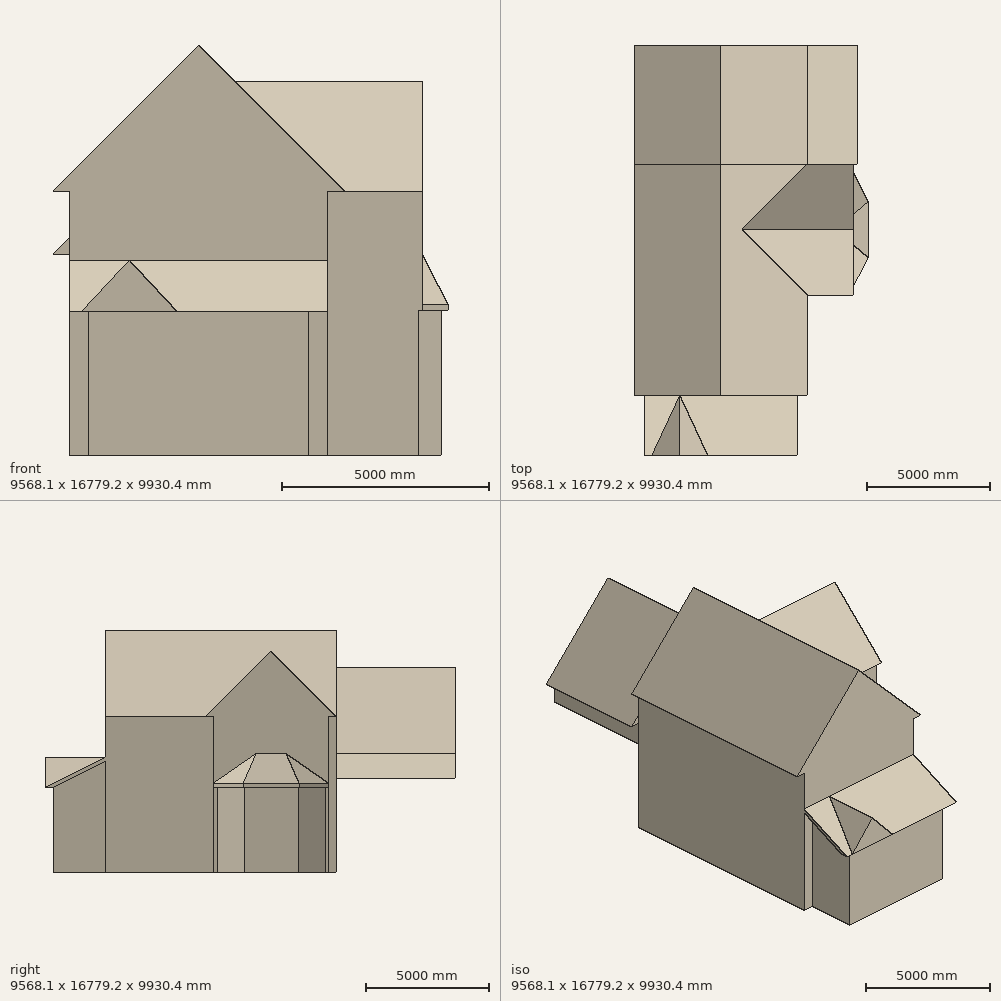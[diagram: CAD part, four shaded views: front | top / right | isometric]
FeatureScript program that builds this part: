
annotation { "Feature Type Name" : "Feature", "Feature Type Description" : "" }
export const myFeature = defineFeature(function(context is Context, id is Id, definition is map)
    precondition{}
    {
        {
            var Q0;
            Q0=qCreatedBy(makeId("Front.planeOp"),FACE);
            var sketch = newSketch(context, id + "F0", { "sketchPlane" : qUnion([Q0])});
            skLineSegment(sketch, "E0", {"start": v(-3529.58, 0) * mm, "end": v(0, 3529.58) * mm});
            skLineSegment(sketch, "E1", {"start": v(0, 3529.58) * mm, "end": v(3529.58, 0) * mm});
            skLineSegment(sketch, "E2", {"start": v(3529.58, 0) * mm, "end": v(-3529.58, 0) * mm});
            skLineSegment(sketch, "E3", {"start": v(0, 0) * mm, "end": v(0, 3529.58) * mm, "construction": true});
            skLineSegment(sketch, "E4", {"start": v(-3124.2, 0) * mm, "end": v(-3124.2, -696.38) * mm, "construction": true});
            skLineSegment(sketch, "E5", {"start": v(-3124.2, -696.38) * mm, "end": v(3124.2, -696.38) * mm, "construction": true});
            skLineSegment(sketch, "E6", {"start": v(3124.2, -696.38) * mm, "end": v(3124.2, 0) * mm, "construction": true});
            skSolve(sketch);
        }
        {
            var Q0;
            Q0=makeQuery(id+"F0.imprint","IMPRINT",FACE,{"disambiguationData":[TD([[makeQuery(id+"F0.imprint","IMPRINT",EDGE,{"derivedFrom":sQuery(id+"F0.wireOp",EDGE,"E0")}),-1.0]])]});
            extrude(context, id + "F1", {"entities" : qUnion([Q0]), "oppositeDirection" : true, "depth" : 9448.8 * mm, "offsetDistance" : 30.48 * mm});
        }
        {
            var Q0;
            Q0=makeQuery(id+"F1.opExtrude","CAP_FACE",FACE,{"disambiguationData":[OSD([sQuery(id+"F0.wireOp",EDGE,"E0"),sQuery(id+"F0.wireOp",EDGE,"E1"),sQuery(id+"F0.wireOp",EDGE,"E2")])],"isStart":false});
            var sketch = newSketch(context, id + "F2", { "sketchPlane" : qUnion([Q0])});
            skLineSegment(sketch, "E7", {"start": v(3529.58, -1524) * mm, "end": v(0, 2005.58) * mm});
            skLineSegment(sketch, "E8", {"start": v(0, 2005.58) * mm, "end": v(-3529.58, -1524) * mm});
            skLineSegment(sketch, "E9", {"start": v(0, 2005.58) * mm, "end": v(0, 3529.58) * mm, "construction": true});
            skLineSegment(sketch, "E10", {"start": v(3529.58, -1524) * mm, "end": v(3529.58, 0) * mm, "construction": true});
            skLineSegment(sketch, "E11", {"start": v(-3529.58, -1524) * mm, "end": v(3529.58, -1524) * mm, "construction": true});
            skLineSegment(sketch, "E12", {"start": v(-3529.58, -1524) * mm, "end": v(-5574.24, -2546.33) * mm});
            skLineSegment(sketch, "E13", {"start": v(-5574.24, -2546.33) * mm, "end": v(3072.38, -2546.33) * mm});
            skLineSegment(sketch, "E14", {"start": v(3072.38, -2546.33) * mm, "end": v(3072.38, -1524) * mm});
            skLineSegment(sketch, "E15", {"start": v(3072.38, -1524) * mm, "end": v(3529.58, -1524) * mm});
            skLineSegment(sketch, "E16", {"start": v(-5269.44, -2546.33) * mm, "end": v(-5269.44, -2393.93) * mm, "construction": true});
            skLineSegment(sketch, "E17", {"start": v(-3529.58, -1524) * mm, "end": v(-3529.58, 0) * mm, "construction": true});
            skSolve(sketch);
        }
        {
            var Q0;
            Q0=qSketchRegion(id+"F2",true);
            extrude(context, id + "F3", {"entities" : qUnion([Q0]), "operationType" : NewBodyOperationType.ADD, "depth" : 4876.8 * mm, "offsetDistance" : 30.48 * mm});
        }
        {
            var Q0;
            Q0=makeQuery(id+"F1.opExtrude","SWEPT_FACE",FACE,{"disambiguationData":[OSD([sQuery(id+"F0.wireOp",EDGE,"E2")])]});
            var sketch = newSketch(context, id + "F4", { "sketchPlane" : qUnion([Q0])});
            skLineSegment(sketch, "E18", {"start": v(-3124.2, 0) * mm, "end": v(-3124.2, -9448.8) * mm});
            skLineSegment(sketch, "E19", {"start": v(-3124.2, -9448.8) * mm, "end": v(3124.2, -9448.8) * mm});
            skLineSegment(sketch, "E20", {"start": v(3124.2, -9448.8) * mm, "end": v(3124.2, 0) * mm});
            skLineSegment(sketch, "E21", {"start": v(3124.2, 0) * mm, "end": v(-3124.2, 0) * mm});
            skLineSegment(sketch, "E22", {"start": v(-3124.2, -4724.4) * mm, "end": v(-3529.58, -4724.4) * mm, "construction": true});
            skLineSegment(sketch, "E23", {"start": v(3124.2, -4724.4) * mm, "end": v(3529.58, -4724.4) * mm, "construction": true});
            skSolve(sketch);
        }
        {
            var Q0;
            Q0=qSketchRegion(id+"F4",true);
            extrude(context, id + "F5", {"entities" : qUnion([Q0]), "operationType" : NewBodyOperationType.ADD, "depth" : 6400.8 * mm, "offsetDistance" : 30.48 * mm});
        }
        {
            var Q0;
            Q0=makeQuery(id+"F5.opExtrude","SWEPT_FACE",FACE,{"disambiguationData":[OSD([sQuery(id+"F4.wireOp",EDGE,"E20")])]});
            var sketch = newSketch(context, id + "F6", { "sketchPlane" : qUnion([Q0])});
            skLineSegment(sketch, "E24", {"start": v(4114.8, 0) * mm, "end": v(6781.8, 2667) * mm});
            skLineSegment(sketch, "E25", {"start": v(6781.8, 2667) * mm, "end": v(9448.8, 0) * mm});
            skLineSegment(sketch, "E26", {"start": v(9448.8, 0) * mm, "end": v(4114.8, 0) * mm});
            skLineSegment(sketch, "E27", {"start": v(6781.8, 0) * mm, "end": v(6781.8, 2667) * mm, "construction": true});
            skSolve(sketch);
        }
        {
            var Q0;
            Q0=qSketchRegion(id+"F6",true);
            var Q1;
            Q1=makeQuery(id+"F1.opExtrude","SWEPT_FACE",FACE,{"disambiguationData":[OSD([sQuery(id+"F0.wireOp",EDGE,"E1")])]});
            extrude(context, id + "F7", {"entities" : qUnion([Q0]), "operationType" : NewBodyOperationType.ADD, "depth" : 2286 * mm, "offsetDistance" : 30.48 * mm, "hasSecondDirection" : true, "secondDirectionBound" : SecondDirectionBoundingType.UP_TO_SURFACE, "secondDirectionOppositeDirection" : true, "secondDirectionDepth" : 30.48 * mm, "secondDirectionBoundEntityFace" : qUnion([Q1])});
        }
        {
            var Q0;
            {var subQ0=sQuery(id+"F0.wireOp",EDGE,"E1");var subQ1=sQuery(id+"F0.wireOp",EDGE,"E2");Q0=makeQuery(id+"F7.boolean.opBoolean","MERGE",FACE,{"derivedFrom":[makeQuery(id+"F5.boolean.opBoolean","SPLIT",FACE,{"disambiguationData":[TD([makeQuery(id+"F1.opExtrude","SWEPT_FACE",FACE,{"disambiguationData":[OSD([subQ0])]})])],"derivedFrom":makeQuery(id+"F1.opExtrude","SWEPT_FACE",FACE,{"disambiguationData":[OSD([subQ1])]})}),makeQuery(id+"F7.opExtrude","SWEPT_FACE",FACE,{"disambiguationData":[OSD([sQuery(id+"F6.wireOp",EDGE,"E26")])]})]});}
            var sketch = newSketch(context, id + "F8", { "sketchPlane" : qUnion([Q0])});
            skLineSegment(sketch, "E28", {"start": v(5410.2, -4419.6) * mm, "end": v(3124.2, -4419.6) * mm});
            skLineSegment(sketch, "E29", {"start": v(3124.2, -4419.6) * mm, "end": v(3124.2, -9144) * mm});
            skLineSegment(sketch, "E30", {"start": v(3124.2, -9144) * mm, "end": v(5410.2, -9144) * mm});
            skLineSegment(sketch, "E31", {"start": v(5410.2, -9144) * mm, "end": v(5410.2, -4419.6) * mm});
            skPoint(sketch, "E32.endSnap0", {"position": v(4267.2, -9144) * mm});
            skLineSegment(sketch, "E33", {"start": v(4267.2, -9448.8) * mm, "end": v(4267.2, -4114.8) * mm, "construction": true});
            skLineSegment(sketch, "E34", {"start": v(4267.2, -6781.8) * mm, "end": v(5410.2, -6781.8) * mm, "construction": true});
            skSolve(sketch);
        }
        {
            var Q0;
            Q0=qSketchRegion(id+"F8",true);
            var Q1;
            Q1=makeQuery(id+"F5.opExtrude","CAP_FACE",FACE,{"disambiguationData":[OSD([sQuery(id+"F4.wireOp",EDGE,"E18"),sQuery(id+"F4.wireOp",EDGE,"E19"),sQuery(id+"F4.wireOp",EDGE,"E20"),sQuery(id+"F4.wireOp",EDGE,"E21")])],"isStart":false});
            extrude(context, id + "F9", {"entities" : qUnion([Q0]), "operationType" : NewBodyOperationType.ADD, "endBound" : BoundingType.UP_TO_SURFACE, "depth" : 30.48 * mm, "endBoundEntityFace" : qUnion([Q1]), "offsetDistance" : 30.48 * mm});
        }
        {
            var Q0;
            {var subQ0=sQuery(id+"F4.wireOp",EDGE,"E21");var subQ1=sQuery(id+"F4.wireOp",EDGE,"E20");Q0=makeQuery(id+"F12.boolean.opBoolean","MERGE",FACE,{"derivedFrom":[makeQuery(id+"F9.boolean.opBoolean","SPLIT",FACE,{"disambiguationData":[TD([makeQuery(id+"F5.opExtrude","SWEPT_FACE",FACE,{"disambiguationData":[OSD([subQ0])]})])],"derivedFrom":makeQuery(id+"F5.opExtrude","SWEPT_FACE",FACE,{"disambiguationData":[OSD([subQ1])]})}),makeQuery(id+"F12.opExtrude","CAP_FACE",FACE,{"disambiguationData":[OSD([sQuery(id+"F11.wireOp",EDGE,"E35"),sQuery(id+"F11.wireOp",EDGE,"E36"),sQuery(id+"F11.wireOp",EDGE,"E37"),sQuery(id+"F11.wireOp",EDGE,"E38"),sQuery(id+"F11.wireOp",EDGE,"E40")])],"isStart":true})]});}
            cPlane(context, id + "F10", {"entities" : qUnion([Q0]), "cplaneType" : CPlaneType.OFFSET, "offset" : 457.2 * mm, "oppositeDirection" : true, "width" : 152.4 * mm, "height" : 152.4 * mm});
        }
        {
            var Q0;
            Q0=qCreatedBy(id+"F10.planeOp",FACE);
            var sketch = newSketch(context, id + "F11", { "sketchPlane" : qUnion([Q0])});
            skLineSegment(sketch, "E35", {"start": v(0, -1676.4) * mm, "end": v(-2453.6, -2903.2) * mm});
            skLineSegment(sketch, "E36", {"start": v(-2453.6, -2903.2) * mm, "end": v(-2133.6, -2903.2) * mm});
            skLineSegment(sketch, "E37", {"start": v(-2133.6, -2903.2) * mm, "end": v(-2133.6, -6400.8) * mm});
            skLineSegment(sketch, "E38", {"start": v(-2133.6, -6400.8) * mm, "end": v(0, -6400.8) * mm});
            skLineSegment(sketch, "E39", {"start": v(-304.8, -1828.8) * mm, "end": v(0, -1828.8) * mm, "construction": true});
            skLineSegment(sketch, "E40", {"start": v(0, -6400.8) * mm, "end": v(0, -1676.4) * mm});
            skSolve(sketch);
        }
        {
            var Q0;
            Q0=qSketchRegion(id+"F11",true);
            var Q1;
            Q1=makeQuery(id+"F5.opExtrude","SWEPT_FACE",FACE,{"disambiguationData":[OSD([sQuery(id+"F4.wireOp",EDGE,"E18")])]});
            extrude(context, id + "F12", {"entities" : qUnion([Q0]), "operationType" : NewBodyOperationType.ADD, "endBound" : BoundingType.UP_TO_SURFACE, "oppositeDirection" : true, "depth" : 30.48 * mm, "endBoundEntityFace" : qUnion([Q1]), "hasOffset" : true, "offsetDistance" : 457.2 * mm});
        }
        {
            var Q0;
            Q0=makeQuery(id+"F12.opExtrude","CAP_FACE",FACE,{"disambiguationData":[OSD([sQuery(id+"F11.wireOp",EDGE,"E35"),sQuery(id+"F11.wireOp",EDGE,"E36"),sQuery(id+"F11.wireOp",EDGE,"E37"),sQuery(id+"F11.wireOp",EDGE,"E38"),sQuery(id+"F11.wireOp",EDGE,"E40")])],"isStart":true});
            var sketch = newSketch(context, id + "F13", { "sketchPlane" : qUnion([Q0])});
            skLineSegment(sketch, "E41.0", {"start": v(0, -1676.4) * mm, "end": v(-2453.6, -2903.2) * mm});
            skLineSegment(sketch, "E42", {"start": v(-2453.6, -2903.2) * mm, "end": v(-2133.6, -2903.2) * mm});
            skLineSegment(sketch, "E43", {"start": v(-2133.6, -2903.2) * mm, "end": v(0, -1836.4) * mm});
            skLineSegment(sketch, "E44", {"start": v(0, -1836.4) * mm, "end": v(0, -1676.4) * mm});
            skSolve(sketch);
        }
        {
            var Q0;
            Q0=qSketchRegion(id+"F13",true);
            var Q1;
            Q1=makeQuery(id+"F5.opExtrude","SWEPT_FACE",FACE,{"disambiguationData":[OSD([sQuery(id+"F4.wireOp",EDGE,"E18")])]});
            extrude(context, id + "F14", {"entities" : qUnion([Q0]), "operationType" : NewBodyOperationType.ADD, "depth" : 457.2 * mm, "offsetDistance" : 30.48 * mm, "hasSecondDirection" : true, "secondDirectionBound" : SecondDirectionBoundingType.UP_TO_SURFACE, "secondDirectionOppositeDirection" : true, "secondDirectionDepth" : 30.48 * mm, "secondDirectionBoundEntityFace" : qUnion([Q1])});
        }
        {
            var Q0;
            Q0=makeQuery(id+"F12.opExtrude","SWEPT_FACE",FACE,{"disambiguationData":[OSD([sQuery(id+"F11.wireOp",EDGE,"E37")])]});
            cPlane(context, id + "F15", {"entities" : qUnion([Q0]), "cplaneType" : CPlaneType.OFFSET, "offset" : 320.04 * mm, "width" : 152.4 * mm, "height" : 152.4 * mm});
        }
        {
            var Q0;
            Q0=qCreatedBy(id+"F15.planeOp",FACE);
            var sketch = newSketch(context, id + "F16", { "sketchPlane" : qUnion([Q0])});
            skLineSegment(sketch, "E45", {"start": v(-2819.4, -2903.2) * mm, "end": v(-1676.4, -1676.4) * mm});
            skLineSegment(sketch, "E46", {"start": v(-1676.4, -1676.4) * mm, "end": v(-533.4, -2903.2) * mm});
            skLineSegment(sketch, "E47", {"start": v(-533.4, -2903.2) * mm, "end": v(-2819.4, -2903.2) * mm});
            skLineSegment(sketch, "E48", {"start": v(-1676.4, -2903.2) * mm, "end": v(-1676.4, -1676.4) * mm, "construction": true});
            skSolve(sketch);
        }
        {
            var Q0;
            Q0=qSketchRegion(id+"F16",true);
            var Q1;
            Q1=makeQuery(id+"F14.boolean.opBoolean","MERGE",FACE,{"derivedFrom":[makeQuery(id+"F12.opExtrude","SWEPT_FACE",FACE,{"disambiguationData":[OSD([sQuery(id+"F11.wireOp",EDGE,"E35")])]}),makeQuery(id+"F14.opExtrude","SWEPT_FACE",FACE,{"disambiguationData":[OSD([sQuery(id+"F13.wireOp",EDGE,"E41.0")])]})]});
            extrude(context, id + "F17", {"entities" : qUnion([Q0]), "operationType" : NewBodyOperationType.ADD, "endBound" : BoundingType.UP_TO_SURFACE, "oppositeDirection" : true, "depth" : 30.48 * mm, "endBoundEntityFace" : qUnion([Q1]), "offsetDistance" : 30.48 * mm});
        }
        {
            var Q0;
            {var subQ0=sQuery(id+"F4.wireOp",EDGE,"E21");var subQ1=sQuery(id+"F4.wireOp",EDGE,"E20");var subQ2=sQuery(id+"F4.wireOp",EDGE,"E19");var subQ3=sQuery(id+"F4.wireOp",EDGE,"E18");Q0=makeQuery(id+"F12.boolean.opBoolean","MERGE",FACE,{"derivedFrom":[makeQuery(id+"F9.boolean.opBoolean","MERGE",FACE,{"derivedFrom":[makeQuery(id+"F5.opExtrude","CAP_FACE",FACE,{"disambiguationData":[OSD([subQ3,subQ2,subQ1,subQ0])],"isStart":false}),makeQuery(id+"F9.opExtrude","CAP_FACE",FACE,{"disambiguationData":[OSD([subQ3,subQ2,subQ1,subQ0])],"isStart":false})]}),makeQuery(id+"F12.opExtrude","SWEPT_FACE",FACE,{"disambiguationData":[OSD([sQuery(id+"F11.wireOp",EDGE,"E38")])]})]});}
            var sketch = newSketch(context, id + "F18", { "sketchPlane" : qUnion([Q0])});
            skLineSegment(sketch, "E49", {"start": v(5410.2, -4419.6) * mm, "end": v(6038.56, -5638.8) * mm});
            skLineSegment(sketch, "E50", {"start": v(6038.56, -5638.8) * mm, "end": v(6038.56, -7924.8) * mm});
            skLineSegment(sketch, "E51", {"start": v(6038.56, -7924.8) * mm, "end": v(5410.2, -9144) * mm});
            skLineSegment(sketch, "E52", {"start": v(5410.2, -9144) * mm, "end": v(5410.2, -4419.6) * mm});
            skLineSegment(sketch, "E53", {"start": v(6038.56, -6781.8) * mm, "end": v(5410.2, -6781.8) * mm, "construction": true});
            skSolve(sketch);
        }
        {
            var Q0;
            Q0=qSketchRegion(id+"F18",true);
            extrude(context, id + "F19", {"entities" : qUnion([Q0]), "operationType" : NewBodyOperationType.ADD, "oppositeDirection" : true, "depth" : 3657.6 * mm, "offsetDistance" : 30.48 * mm});
        }
        {
            var Q0;
            Q0=makeQuery(id+"F9.opExtrude","SWEPT_FACE",FACE,{"disambiguationData":[OSD([sQuery(id+"F8.wireOp",EDGE,"E28")])]});
            cPlane(context, id + "F20", {"entities" : qUnion([Q0]), "cplaneType" : CPlaneType.OFFSET, "offset" : 1219.2 * mm, "oppositeDirection" : true, "width" : 152.4 * mm, "height" : 152.4 * mm});
        }
        {
            var Q0;
            Q0=qCreatedBy(id+"F20.planeOp",FACE);
            var sketch = newSketch(context, id + "F21", { "sketchPlane" : qUnion([Q0])});
            skLineSegment(sketch, "E54", {"start": v(6038.56, -2743.2) * mm, "end": v(5410.2, -1524) * mm});
            skLineSegment(sketch, "E55", {"start": v(5410.2, -1524) * mm, "end": v(5410.2, -2743.2) * mm});
            skLineSegment(sketch, "E56", {"start": v(5410.2, -2743.2) * mm, "end": v(6038.56, -2743.2) * mm});
            skSolve(sketch);
        }
        {
            var Q0;
            Q0=qSketchRegion(id+"F21",true);
            extrude(context, id + "F22", {"entities" : qUnion([Q0]), "operationType" : NewBodyOperationType.ADD, "oppositeDirection" : true, "depth" : 2286 * mm, "offsetDistance" : 30.48 * mm});
        }
        {
            var Q0;
            Q0=makeQuery(id+"F19.opExtrude","SWEPT_FACE",FACE,{"disambiguationData":[OSD([sQuery(id+"F18.wireOp",EDGE,"E50")])]});
            var sketch = newSketch(context, id + "F23", { "sketchPlane" : qUnion([Q0])});
            skLineSegment(sketch, "E57", {"start": v(5638.8, -2743.2) * mm, "end": v(6172.2, -1524) * mm});
            skLineSegment(sketch, "E58", {"start": v(6172.2, -1524) * mm, "end": v(5638.8, -1524) * mm});
            skLineSegment(sketch, "E59", {"start": v(5638.8, -1524) * mm, "end": v(5638.8, -2743.2) * mm});
            skLineSegment(sketch, "E60", {"start": v(6781.8, -2743.2) * mm, "end": v(6781.8, -1660.14) * mm, "construction": true});
            skLineSegment(sketch, "E61.MirrorCS", {"start": v(7924.8, -1524) * mm, "end": v(7924.8, -2743.2) * mm});
            skLineSegment(sketch, "E62.MirrorCS", {"start": v(7924.8, -2743.2) * mm, "end": v(7391.4, -1524) * mm});
            skLineSegment(sketch, "E63.MirrorCS", {"start": v(7391.4, -1524) * mm, "end": v(7924.8, -1524) * mm});
            skSolve(sketch);
        }
        {
            var Q0;
            Q0=qSketchRegion(id+"F23",true);
            var Q1;
            Q1=makeQuery(id+"F9.boolean.opBoolean","MERGE",FACE,{"derivedFrom":[makeQuery(id+"F7.opExtrude","CAP_FACE",FACE,{"disambiguationData":[OSD([sQuery(id+"F6.wireOp",EDGE,"E24"),sQuery(id+"F6.wireOp",EDGE,"E25"),sQuery(id+"F6.wireOp",EDGE,"E26")])],"isStart":false}),makeQuery(id+"F9.opExtrude","SWEPT_FACE",FACE,{"disambiguationData":[OSD([sQuery(id+"F8.wireOp",EDGE,"E31")])]})]});
            extrude(context, id + "F24", {"entities" : qUnion([Q0]), "operationType" : NewBodyOperationType.REMOVE, "endBound" : BoundingType.UP_TO_SURFACE, "oppositeDirection" : true, "depth" : 30.48 * mm, "endBoundEntityFace" : qUnion([Q1]), "offsetDistance" : 30.48 * mm});
        }
        {
            var Q1;
            {var subQ1=sQuery(id+"F18.wireOp",EDGE,"E49");var subQ2=sQuery(id+"F18.wireOp",EDGE,"E50");Q1=makeQuery(id+"F22.boolean.opBoolean","SPLIT",FACE,{"disambiguationData":[TD([makeQuery(id+"F9.opExtrude","SWEPT_FACE",FACE,{"disambiguationData":[OSD([sQuery(id+"F8.wireOp",EDGE,"E28")])]})])],"derivedFrom":makeQuery(id+"F19.opExtrude","CAP_FACE",FACE,{"disambiguationData":[OSD([subQ1,subQ2,sQuery(id+"F18.wireOp",EDGE,"E51"),sQuery(id+"F18.wireOp",EDGE,"E52")])],"isStart":false})});}
            var Q2;
            Q2=makeQuery(id+"F24.boolean.opBoolean","COPY",VERTEX,{"derivedFrom":makeQuery(id+"F24.opExtrude","CAP_VERTEX",VERTEX,{"disambiguationData":[OSD([sQuery(id+"F6.wireOp",EDGE,"E24"),sQuery(id+"F6.wireOp",EDGE,"E25"),sQuery(id+"F6.wireOp",EDGE,"E26"),sQuery(id+"F8.wireOp",EDGE,"E31"),sQuery(id+"F23.wireOp",EDGE,"E57"),sQuery(id+"F23.wireOp",EDGE,"E58")])],"isStart":false})});
            loft(context, id + "F25", {"operationType" : NewBodyOperationType.ADD, "sheetProfilesArray" : [{ "sheetProfileEntities" : qUnion([Q1]) }, { "sheetProfileEntities" : qUnion([Q2]) }]});
        }
        {
            var Q1;
            {var subQ0=sQuery(id+"F18.wireOp",EDGE,"E50");var subQ2=sQuery(id+"F18.wireOp",EDGE,"E51");Q1=makeQuery(id+"F22.boolean.opBoolean","SPLIT",FACE,{"disambiguationData":[TD([makeQuery(id+"F9.opExtrude","SWEPT_FACE",FACE,{"disambiguationData":[OSD([sQuery(id+"F8.wireOp",EDGE,"E30")])]})])],"derivedFrom":makeQuery(id+"F19.opExtrude","CAP_FACE",FACE,{"disambiguationData":[OSD([sQuery(id+"F18.wireOp",EDGE,"E49"),subQ0,subQ2,sQuery(id+"F18.wireOp",EDGE,"E52")])],"isStart":false})});}
            var Q2;
            Q2=makeQuery(id+"F24.boolean.opBoolean","COPY",VERTEX,{"derivedFrom":makeQuery(id+"F24.opExtrude","CAP_VERTEX",VERTEX,{"disambiguationData":[OSD([sQuery(id+"F6.wireOp",EDGE,"E24"),sQuery(id+"F6.wireOp",EDGE,"E25"),sQuery(id+"F6.wireOp",EDGE,"E26"),sQuery(id+"F8.wireOp",EDGE,"E31"),sQuery(id+"F23.wireOp",EDGE,"E62.MirrorCS"),sQuery(id+"F23.wireOp",EDGE,"E63.MirrorCS")])],"isStart":false})});
            loft(context, id + "F26", {"operationType" : NewBodyOperationType.ADD, "sheetProfilesArray" : [{ "sheetProfileEntities" : qUnion([Q1]) }, { "sheetProfileEntities" : qUnion([Q2]) }]});
        }
        {
            var Q0;
            {var subQ0=sQuery(id+"F4.wireOp",EDGE,"E21");var subQ1=sQuery(id+"F4.wireOp",EDGE,"E20");var subQ2=sQuery(id+"F4.wireOp",EDGE,"E19");var subQ3=sQuery(id+"F4.wireOp",EDGE,"E18");Q0=makeQuery(id+"F19.boolean.opBoolean","MERGE",FACE,{"derivedFrom":[makeQuery(id+"F12.boolean.opBoolean","MERGE",FACE,{"derivedFrom":[makeQuery(id+"F9.boolean.opBoolean","MERGE",FACE,{"derivedFrom":[makeQuery(id+"F5.opExtrude","CAP_FACE",FACE,{"disambiguationData":[OSD([subQ3,subQ2,subQ1,subQ0])],"isStart":false}),makeQuery(id+"F9.opExtrude","CAP_FACE",FACE,{"disambiguationData":[OSD([subQ3,subQ2,subQ1,subQ0])],"isStart":false})]}),makeQuery(id+"F12.opExtrude","SWEPT_FACE",FACE,{"disambiguationData":[OSD([sQuery(id+"F11.wireOp",EDGE,"E38")])]})]}),makeQuery(id+"F19.opExtrude","CAP_FACE",FACE,{"disambiguationData":[OSD([sQuery(id+"F18.wireOp",EDGE,"E49"),sQuery(id+"F18.wireOp",EDGE,"E50"),sQuery(id+"F18.wireOp",EDGE,"E51"),sQuery(id+"F18.wireOp",EDGE,"E52")])],"isStart":true})]});}
            var sketch = newSketch(context, id + "F27", { "sketchPlane" : qUnion([Q0])});
            skLineSegment(sketch, "E64.0", {"start": v(5886.16, -7887.84) * mm, "end": v(5317.3, -8991.6) * mm});
            skLineSegment(sketch, "E64.1", {"start": v(5886.16, -5675.76) * mm, "end": v(5886.16, -7887.84) * mm});
            skLineSegment(sketch, "E64.2", {"start": v(5317.3, -4572) * mm, "end": v(5886.16, -5675.76) * mm});
            skLineSegment(sketch, "E65", {"start": v(5317.3, -8991.6) * mm, "end": v(5317.3, -9144) * mm});
            skLineSegment(sketch, "E66", {"start": v(5317.3, -4572) * mm, "end": v(5317.3, -4419.6) * mm});
            skLineSegment(sketch, "E67", {"start": v(5317.3, -4572) * mm, "end": v(5317.3, -8991.6) * mm, "construction": true});
            skLineSegment(sketch, "E68.0", {"start": v(6038.56, -7924.8) * mm, "end": v(5410.2, -9144) * mm});
            skLineSegment(sketch, "E69.0", {"start": v(6038.56, -5638.8) * mm, "end": v(6038.56, -7924.8) * mm});
            skLineSegment(sketch, "E70.0", {"start": v(5410.2, -4419.6) * mm, "end": v(6038.56, -5638.8) * mm});
            skLineSegment(sketch, "E71", {"start": v(5317.3, -4419.6) * mm, "end": v(5410.2, -4419.6) * mm});
            skLineSegment(sketch, "E72", {"start": v(5317.3, -9144) * mm, "end": v(5410.2, -9144) * mm});
            skSolve(sketch);
        }
        {
            var Q0;
            Q0=qSketchRegion(id+"F27",true);
            var Q1;
            {var subQ0=sQuery(id+"F23.wireOp",EDGE,"E59");var subQ1=sQuery(id+"F23.wireOp",EDGE,"E57");var subQ2=sQuery(id+"F21.wireOp",EDGE,"E56");var subQ3=sQuery(id+"F21.wireOp",EDGE,"E54");var subQ4=sQuery(id+"F18.wireOp",EDGE,"E50");var subQ5=sQuery(id+"F18.wireOp",EDGE,"E49");Q1=makeQuery(id+"F25.boolean.opBoolean","MERGE",VERTEX,{"derivedFrom":[makeQuery(id+"F24.boolean.opBoolean","MERGE",VERTEX,{"derivedFrom":[makeQuery(id+"F22.boolean.opBoolean","MERGE",VERTEX,{"derivedFrom":[makeQuery(id+"F19.opExtrude","CAP_VERTEX",VERTEX,{"disambiguationData":[OSD([subQ5,subQ4])],"isStart":false}),makeQuery(id+"F22.opExtrude","CAP_VERTEX",VERTEX,{"disambiguationData":[OSD([subQ3,subQ2])],"isStart":true})]}),makeQuery(id+"F24.opExtrude","CAP_VERTEX",VERTEX,{"disambiguationData":[OSD([subQ5,subQ4,subQ3,subQ2,subQ1,subQ0])],"isStart":true})]}),makeQuery(id+"F25.opLoft","MID_CAP_VERTEX",VERTEX,{"disambiguationData":[OSD([subQ5,subQ4,subQ3,subQ2,subQ1,subQ0])],"capPos":0.0})]});}
            extrude(context, id + "F28", {"entities" : qUnion([Q0]), "operationType" : NewBodyOperationType.REMOVE, "endBound" : BoundingType.UP_TO_VERTEX, "oppositeDirection" : true, "depth" : 30.48 * mm, "endBoundEntityVertex" : qUnion([Q1]), "hasOffset" : true, "offsetDistance" : 152.4 * mm});
        }
    });
